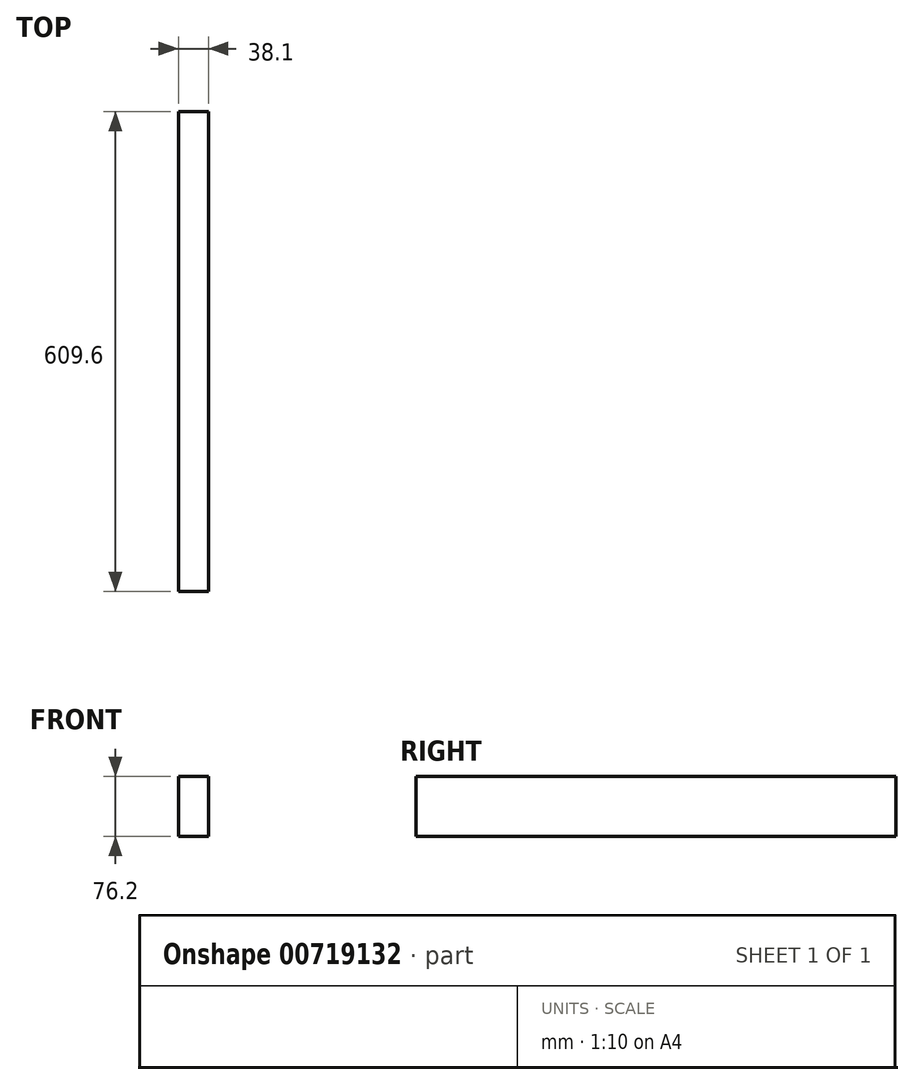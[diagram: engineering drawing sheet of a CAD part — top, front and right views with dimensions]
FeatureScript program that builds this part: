
annotation { "Feature Type Name" : "Feature", "Feature Type Description" : "" }
export const myFeature = defineFeature(function(context is Context, id is Id, definition is map)
    precondition{}
    {
        {
            var Q0;
            Q0=qCreatedBy(makeId("Front.planeOp"),FACE);
            var sketch = newSketch(context, id + "F0", { "sketchPlane" : qUnion([Q0])});
            skLineSegment(sketch, "E0.bottom", {"start": v(0, 0) * mm, "end": v(-38.1, 0) * mm});
            skLineSegment(sketch, "E0.top", {"start": v(0, 76.2) * mm, "end": v(-38.1, 76.2) * mm});
            skLineSegment(sketch, "E0.left", {"start": v(0, 0) * mm, "end": v(0, 76.2) * mm});
            skLineSegment(sketch, "E0.right", {"start": v(-38.1, 0) * mm, "end": v(-38.1, 76.2) * mm});
            skSolve(sketch);
        }
        {
            var Q0;
            Q0 = qSketchRegion(id + "F0", true);
            extrude(context, id + "F1", {"entities" : qUnion([Q0]), "depth" : 609.6 * mm, "offsetDistance" : 25.4 * mm});
        }
    });
